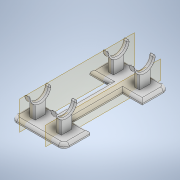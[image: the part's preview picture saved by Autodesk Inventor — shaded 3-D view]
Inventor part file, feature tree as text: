
AUTODESK INVENTOR PART (.ipt)
format: ipt  version: 2022 (Build 260153000, 153)  size: 318,464 bytes
history: native  units: in
note: dims shown in document units (in); Inventor stores cm internally (conversion verified against a paired STEP export)
features: extrude x5, sketch x5, fillet x3, plane x2
ambient origin geometry x8: Origin, YZ Plane, XZ Plane, XY Plane, X Axis, Y Axis, Z Axis, Center Point
bodies: Solid1 (feature_tree)
feature tree (15):
  extrude  "Extrusion1"  Depth=15.748in
  extrude  "Extrusion2"  Depth=0.5906in TaperAngle=0.0deg
  fillet  "Fillet1"  Radius=2.9528in
  extrude  "Extrusion3"  Depth=2.9528in
  plane  "Work Plane1"
  extrude  "Extrusion4"  Depth=0.3937in
  plane  "Work Plane2"
  extrude  "Extrusion5"  Depth=1.5748in
  fillet  "Fillet2"  Radius=1.5748in
  fillet  "Fillet3"  Radius=1.9685in
  sketch  "Sketch1"  dims[d0=7.874in d1=15.748in]
  sketch  "Sketch3"  dims[d2=0.7874in d3=0.5906in d4=0.0in d5=2.9528in]
  sketch  "Sketch5"  dims[d6=7.874in d7=2.9528in]
  sketch  "Sketch6"  dims[d8=0.5906in d9=0.0in d10=0.3937in]
  sketch  "Sketch7"  dims[d11=0.7874in d12=1.5748in d13=1.5748in d14=1.9685in d15=0.0in d16=1.9685in d17=0.7874in d18=0.0in d19=-1.9685in d20=0.7874in d21=0.0in d22=0.1969in d23=0.1969in]
